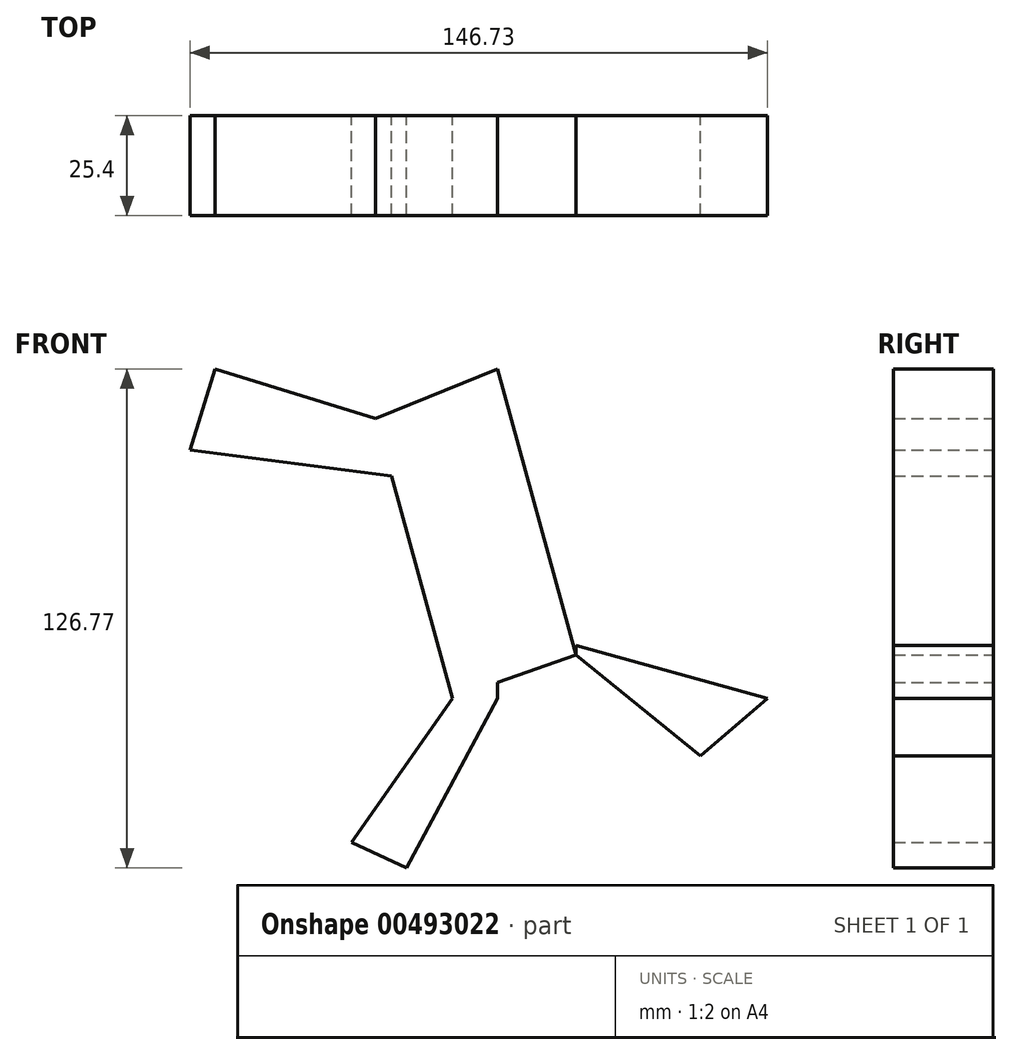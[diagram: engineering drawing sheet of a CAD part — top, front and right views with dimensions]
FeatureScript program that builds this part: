
annotation { "Feature Type Name" : "Feature", "Feature Type Description" : "" }
export const myFeature = defineFeature(function(context is Context, id is Id, definition is map)
    precondition{}
    {
        {
            var Q0;
            Q0=qCreatedBy(makeId("Front.planeOp"),FACE);
            var sketch = newSketch(context, id + "F0", { "sketchPlane" : qUnion([Q0])});
            skLineSegment(sketch, "E0", {"start": v(-37.54, 31.17) * mm, "end": v(-17.97, -39.94) * mm});
            skLineSegment(sketch, "E1", {"start": v(-37.54, 31.17) * mm, "end": v(-6.6, 43.7) * mm});
            skLineSegment(sketch, "E2", {"start": v(-6.6, 43.7) * mm, "end": v(13.4, -28.98) * mm});
            skLineSegment(sketch, "E3", {"start": v(13.4, -28.98) * mm, "end": v(-17.97, -39.94) * mm});
            skLineSegment(sketch, "E4", {"start": v(-6.6, 43.7) * mm, "end": v(24.97, 81.03) * mm});
            skLineSegment(sketch, "E5", {"start": v(24.97, 81.03) * mm, "end": v(36.9, 75.32) * mm});
            skLineSegment(sketch, "E6", {"start": v(36.9, 75.32) * mm, "end": v(0, 31.17) * mm});
            skLineSegment(sketch, "E7", {"start": v(-37.54, 31.17) * mm, "end": v(-78.33, 43.7) * mm});
            skLineSegment(sketch, "E8", {"start": v(-78.33, 43.7) * mm, "end": v(-84.67, 23.08) * mm});
            skLineSegment(sketch, "E9", {"start": v(-84.67, 23.08) * mm, "end": v(-33.51, 16.53) * mm});
            skLineSegment(sketch, "E10", {"start": v(-33.51, 16.53) * mm, "end": v(-17.97, -39.94) * mm});
            skLineSegment(sketch, "E11", {"start": v(-17.97, -39.94) * mm, "end": v(-43.67, -76.57) * mm});
            skLineSegment(sketch, "E12", {"start": v(-43.67, -76.57) * mm, "end": v(-29.65, -83.07) * mm});
            skLineSegment(sketch, "E13", {"start": v(-29.65, -83.07) * mm, "end": v(-6.6, -39.94) * mm});
            skLineSegment(sketch, "E14", {"start": v(-6.6, -39.94) * mm, "end": v(-6.6, -34.46) * mm});
            skPoint(sketch, "E14.endSnap0", {"position": v(-2.28, -34.46) * mm});
            skLineSegment(sketch, "E15", {"start": v(-4.37, -35.85) * mm, "end": v(13.4, -30.95) * mm});
            skLineSegment(sketch, "E16", {"start": v(13.4, -30.95) * mm, "end": v(13.4, -28.98) * mm});
            skLineSegment(sketch, "E17", {"start": v(13.4, -28.98) * mm, "end": v(45.02, -54.64) * mm});
            skLineSegment(sketch, "E18", {"start": v(45.02, -54.64) * mm, "end": v(62.06, -39.94) * mm});
            skLineSegment(sketch, "E19", {"start": v(62.06, -39.94) * mm, "end": v(13.4, -26.52) * mm});
            skLineSegment(sketch, "E20", {"start": v(13.4, -26.52) * mm, "end": v(13.4, -28.98) * mm});
            skSolve(sketch);
        }
        {
            var Q0;
            Q0=makeQuery(id+"F0.imprint","IMPRINT",FACE,{"disambiguationData":[TD([[makeQuery(id+"F0.imprint","IMPRINT",EDGE,{"derivedFrom":sQuery(id+"F0.wireOp",EDGE,"E17")}),1.0]])]});
            var Q1;
            Q1=makeQuery(id+"F0.imprint","IMPRINT",FACE,{"disambiguationData":[TD([[makeQuery(id+"F0.imprint","IMPRINT",EDGE,{"derivedFrom":sQuery(id+"F0.wireOp",EDGE,"E0")}),-1.0]])]});
            var Q2;
            {var subQ1=sQuery(id+"F0.wireOp",EDGE,"E11");Q2=makeQuery(id+"F0.imprint","IMPRINT",FACE,{"disambiguationData":[TD([[makeQuery(id+"F0.imprint","IMPRINT",EDGE,{"derivedFrom":subQ1}),1.0]])]});}
            var Q3;
            Q3=makeQuery(id+"F0.imprint","IMPRINT",FACE,{"disambiguationData":[TD([[makeQuery(id+"F0.imprint","IMPRINT",EDGE,{"derivedFrom":sQuery(id+"F0.wireOp",EDGE,"E0")}),1.0]])]});
            extrude(context, id + "F1", {"entities" : qUnion([Q0, Q1, Q2, Q3]), "depth" : 25.4 * mm});
        }
    });
